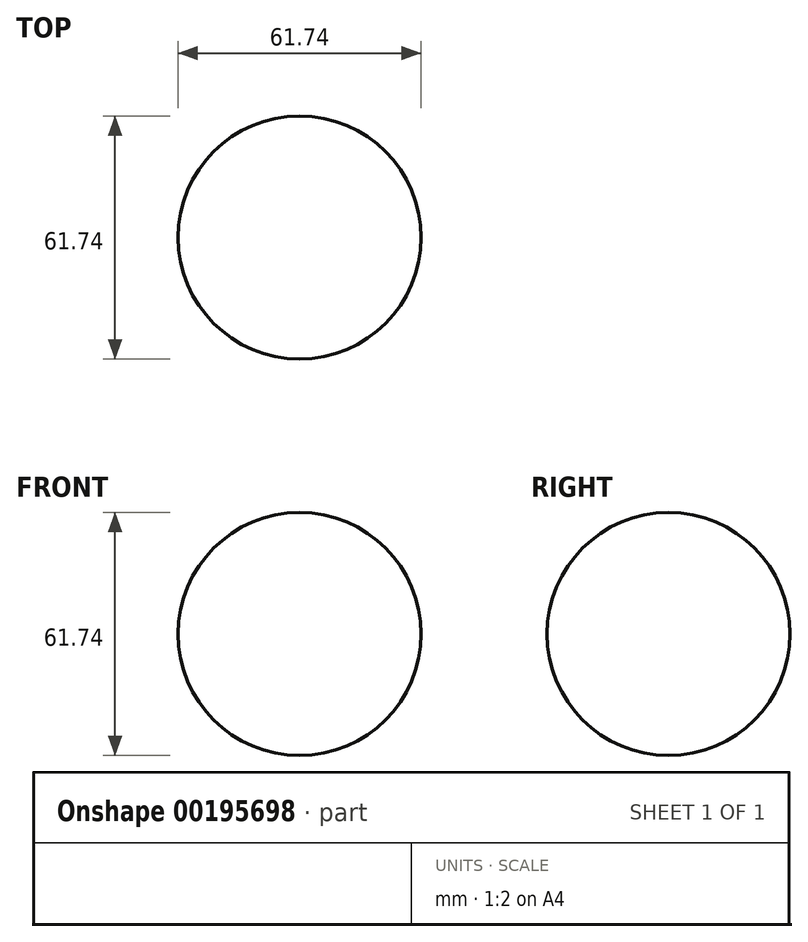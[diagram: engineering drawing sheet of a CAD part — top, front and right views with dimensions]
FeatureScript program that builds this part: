
annotation { "Feature Type Name" : "Feature", "Feature Type Description" : "" }
export const myFeature = defineFeature(function(context is Context, id is Id, definition is map)
    precondition{}
    {
        {
            var Q0;
            Q0=qCreatedBy(makeId("Top.planeOp"),FACE);
            var sketch = newSketch(context, id + "F0", { "sketchPlane" : qUnion([Q0])});
            skArc(sketch, "E0", {"start": v(0, 30.87) * mm, "mid": v(-30.87, 0) * mm, "end": v(0, -30.87) * mm});
            skLineSegment(sketch, "E1", {"start": v(0, 37.67) * mm, "end": v(0, -37.67) * mm, "construction": true});
            skLineSegment(sketch, "E2", {"start": v(0, 30.87) * mm, "end": v(0, -30.87) * mm});
            skSolve(sketch);
        }
        {
            var Q0;
            Q0=makeQuery(id+"F0.imprint","IMPRINT",FACE,{"disambiguationData":[TD([[makeQuery(id+"F0.imprint","IMPRINT",EDGE,{"derivedFrom":sQuery(id+"F0.wireOp",EDGE,"E0")}),1.0]])]});
            var Q1;
            Q1=sQuery(id+"F0.wireOp",EDGE,"E1");
            revolve(context, id + "F1", {"entities" : qUnion([Q0]), "axis" : qUnion([Q1]), "revolveType" : RevolveType.FULL});
        }
    });
